# Revit family: Стеллаж передвижной архивный ДиКом
name_source: partatom
category: Оборудование
revit_build: Autodesk Revit 2017 (Build: 20170419_0315(x64)
units: mm (PartAtom-declared; Revit-internal decimal feet)

## family parameters
Всегда вертикально = Да
На основе рабочей плоскости = Нет
Общий = Нет
При загрузке вырезать с полостями = Нет
Размер круглого соединителя = Использовать диаметр
Тип детали = Нормальный
Точка расчета площади = Нет

## types (2) — shared parameters
Глубина = 3040 мм
Единицы = компл.
Завод = ДиКом
Масса = 1500
Материал = Металл окрашенный светло-серый
Обозначение = СДМ
Ширина = 5800 мм

## per-type parameters (varying)
| type | Высота | Группа модели | Изготовитель | Наименование |
| 2290мм | 2290 мм | ТХ |  | Стеллаж передвижной с ручным приводом, 7 мобильных рядов по 3 метровых секции, 5 полок |
| 2625мм | 2625 мм |  | Severin | Стеллаж передвижной с ручным приводом, 7 мобильных рядов по 3 метровых секции, 6 полок |

## geometry (parser evidence)
native form markers: Blend x6
no freeform markers — native parametric forms only
